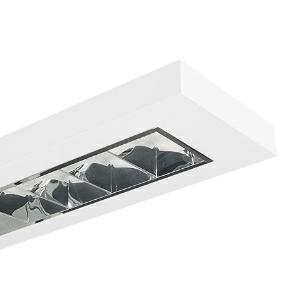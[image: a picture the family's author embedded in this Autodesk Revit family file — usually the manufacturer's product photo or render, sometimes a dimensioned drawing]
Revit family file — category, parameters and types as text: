
# Revit family: 3f_filippi_-_3f_travetta_tunable_white_2mg_3f_filippi_-_10763_-_3f_trav__led_2x22w_dali_dt8_tw_2mg_l1590__cct_4000__6253
name_source: partatom
category: Lighting Fixtures
units: mm (PartAtom-declared; Revit-internal decimal feet)

## family parameters
Cut with Voids When Loaded = No
Host = Face
Light Source = No
Part Type = Normal
Room Calculation Point = No
Round Connector Dimension = Use Diameter
Shared = No

## types (1)
- 3F Filippi - 3F Travetta Tunable White 2MG (1 x LED, 6236 lm, 50 W, 4000 K)
    Apparent Load = 50 VA
    Approval mark = ENEC
    CIE Flux Codes = 72 99 100 100 100
    Color Rendering = 80
    Color Temperature = 4000 K
    Control Gear = Electronic transformer
    Default Elevation = 1800 mm
    Description = ILLUMINOTECHNICAL
Luminous efficiency 100% (DLOR 100%, ULOR 0%).
Luminaire luminous flux 5800 lm @ 2700 K.
Luminaire luminous flux 6236 lm @ 4000 K.
Luminaire luminous flux 6236 lm @ 6500 K.
Direct symmetric distribution.
Installation Interdistance Transv.D = 1.29 x hu - Long.D = 1.23 x hu.
Average luminance <1000 cd/m² for radial angles >65°.
Tabular UGR (CIE 117 - 4H-8H; S=0.25H; 70/50/20): RUG 17.1 - 19.3.
Beam angle: 80° - 84°.
Luminous efficacy 125 lm/W.
Lifetime (L90/B10): 30000 h. (tq+25°C)
Lifetime (L85/B10): 50000 h. (tq+25°C)
Lifetime (L75/B10): 80000 h. (tq+25°C)
Lifetime (L70/B10): 100000 h. (tq+25°C)
Sudden decreased luminous flux after 50000 hours: 0% (C0).
Photobiological safety in compliance with IEC/TR 62778: RG0 risk exempt, (IEC 62471).
In compliance with IEC/EN 62722-2-1 - IEC/EN 62717 standards.

SOURCE
2 linear LED modules 22W/TW.
Energy efficiency class (UE 2019/2020 - UE 2019/2015): D.
CIE 13.3 Colour rendering index: CRI >80 (R9 <50%).
IES TM-30 Fidelity Index: Rf = 84 Rg = 95.
The colour temperature can be adjusted between 2700 K and 6500 K.
Colour initial tolerance (MacAdam): SDCM 2.

MECHANICAL
Housing with squared shape in white painted galvannealed steel, with nonreflecting surface.
2MG parabolic louvre, high efficiency, in specular aluminium with superficial titanium-magnesium treatment, non-iridescent, with transverse blades closed at the top.
Prismatic flat diffuser in transparent methacrylate (PMMA), multilenticular, anti-glare, prismatic exterior, placed above louvre blades.
Film protective against dust and finger marks, adhesive, attached to louvre.
Luminaire with limited surface temperature. - D - (EN 60598-2-24)
Dimensions: 1590x190 mm, height 60 mm (edge 40 mm). Weight 5.35 kg.
IP20 protection degree.
Mechanical strength to impacts IK02 (0.2 joule).
Glow-wire test resistance 650°C.

ELECTRICAL
Halogen Free DALI DT8, PUSH-DIM, electronic wiring 230V-50/60Hz, power factor 0.95, THD <25%, constant output power, SELV, class I, 1 driver, 1 DALI addresse.
Power of the luminaire 50 W.
CE - IEC 60598-1 - EN 60598-1.
SAFE FLICKER: PstLM=<1 and SVM=<0.4 (IEC TR 61547-1 and IEC TR 63158), to ensure a more comfortable and safe light.
Luminaire compliant with EN 60598-2-22 for power supply from a centralised emergency system CPSS (Central Power Supply System), not incorporated in the luminaire - high risk areas excluded. The default power and flux are 100% in AC and 15% in DC.
Ambient temperature from 0°C to +25°C.
Temperature class T6 max 85°C.
5-pole terminal block (L-N-PE-DA/DA) for line connection with connection capacity 2x2.5 mm².
Relative humidity UR: <85%.

INSTALLATION
Suspended.
All accessories dedicated to this product are available on the Catalog and on our website www.3F-Filippi.com.

APPLICATIONS
Any environments requiring light which aims for the wellness of people.
In environments, even with reduced height, requiring a comfortable light. Offices with VDTs, managerial offices and staterooms.

LIGHT MANAGEMENT
Recommended minimum setting: 10%.
The luminaire, equipped with DALI DT8 driver, is designed for adjusting the luminous flux and colour temperature; can be controlled manually or automatically/manually with 3F HCL technology or 3F Bluetooth.

WARNING
Luminaire designed for disposal/recycling at end-of-life.
Replaceable (LED only) light source by a professional. Replaceable control gear by a professional.
    Height = 60 mm  [stored 0.19685 ft]
    Lamp = 1 x LED
    Lamp Light Flux = 6236 lm
    Lamp Power = 50 W
    Lamp count = 1
    Length = 1590 mm
    Lifetime = 50000 h
    Luminous efficacy = 125 lm/W
    Manufacturer = 3F Filippi
    ModVariant = No
    Model = 3F Filippi - 10763 - 3F TRAV. LED 2X22W DALI DT8 TW 2MG L1590 (CCT 4000)
    Mounting Place = Ceiling
    Mounting Type = Pendant
    Number of Poles = 1
    OnlyDefault = Yes
    Power Factor = 1
    Product Name = 3F Filippi - 3F Travetta Tunable White 2MG
    Product group = pendant luminaire
    ProductGroupID = 9
    Protection Class = Protection class I
    Protection Degree = IP 20
    RLX_Detail_Level = 1
    RLX_Emergency_Light_Flux = 0 lm
    RLX_Emergency_Type = 0
    RLX_Emergency_Type_DB = No
    RlxData = <blob elided: 56517 chars, md5=c520c655>
    Socket = socket
    Standby Power = 0 W
    System Light Flux = 6236 lm
    System Power = 50 W
    Type Comments = Product without accessories
    Type Image = 3ffilippi_3f_travetta_led_2mg.jpg
    URL = http://relux.com
    VarID = ---
    Voltage = 0 V
    Weight = 0.00 kg
    Width = 190 mm  [stored 0.62336 ft]

note: [stored X ft] marks values corroborated as IEEE doubles in the binary element streams (Revit-internal decimal feet)

## geometry (parser evidence)
native form markers: Blend x4, Sweep x13
no freeform markers — native parametric forms only
